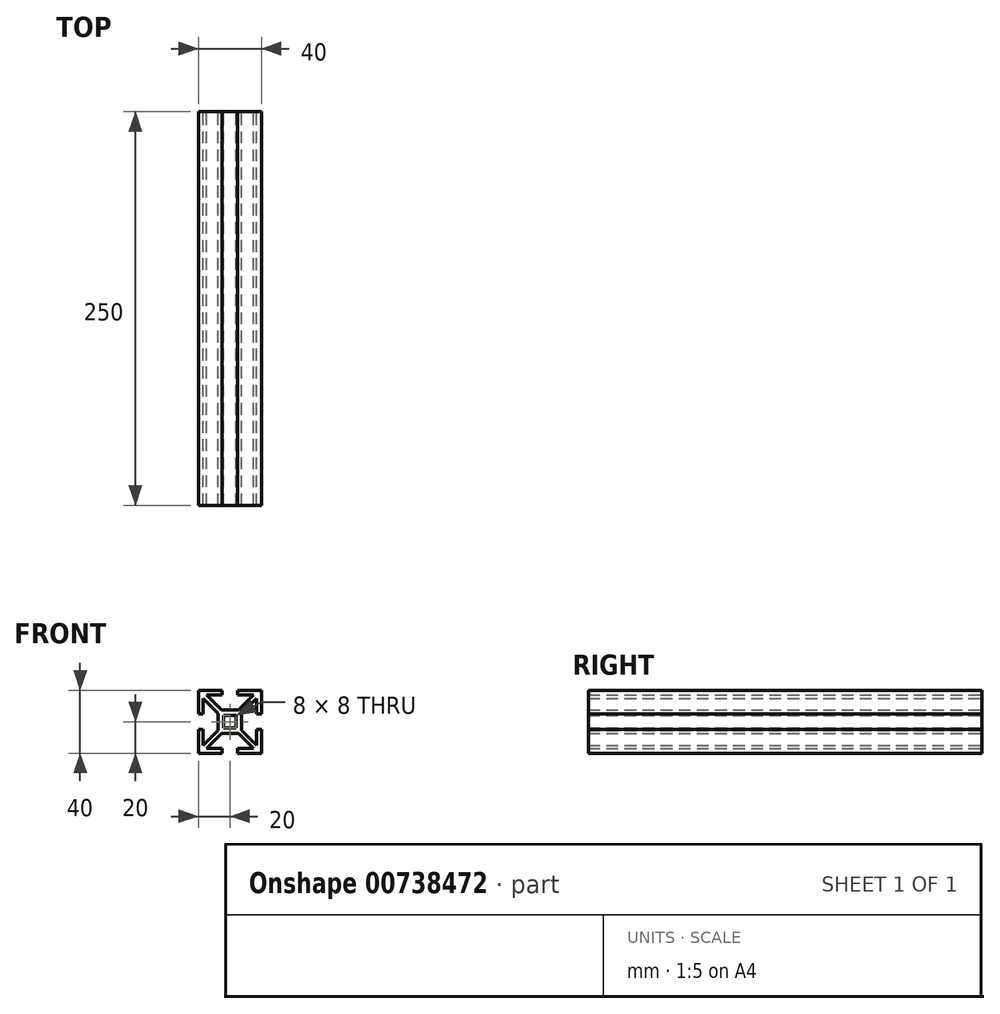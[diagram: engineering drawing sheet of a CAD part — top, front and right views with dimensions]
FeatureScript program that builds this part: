
annotation { "Feature Type Name" : "Feature", "Feature Type Description" : "" }
export const myFeature = defineFeature(function(context is Context, id is Id, definition is map)
    precondition{}
    {
        {
            var Q0;
            Q0=qCreatedBy(makeId("Front.planeOp"),FACE);
            var sketch = newSketch(context, id + "F0", { "sketchPlane" : qUnion([Q0])});
            skPoint(sketch, "E0.middle", {"position": v(0, 0) * mm});
            skLineSegment(sketch, "E1.bottom", {"start": v(20, 20) * mm, "end": v(-20, 20) * mm});
            skLineSegment(sketch, "E1.top", {"start": v(20, -20) * mm, "end": v(-20, -20) * mm});
            skLineSegment(sketch, "E1.left", {"start": v(20, 20) * mm, "end": v(20, -20) * mm});
            skLineSegment(sketch, "E1.right", {"start": v(-20, 20) * mm, "end": v(-20, -20) * mm});
            skLineSegment(sketch, "E2.bottom", {"start": v(4, 4) * mm, "end": v(-4, 4) * mm});
            skLineSegment(sketch, "E2.top", {"start": v(4, -4) * mm, "end": v(-4, -4) * mm});
            skLineSegment(sketch, "E2.left", {"start": v(4, 4) * mm, "end": v(4, -4) * mm});
            skLineSegment(sketch, "E2.right", {"start": v(-4, 4) * mm, "end": v(-4, -4) * mm});
            skLineSegment(sketch, "E3.bottom", {"start": v(7.5, -7.5) * mm, "end": v(-7.5, -7.5) * mm});
            skLineSegment(sketch, "E3.top", {"start": v(7.5, 7.5) * mm, "end": v(-7.5, 7.5) * mm});
            skLineSegment(sketch, "E3.left", {"start": v(7.5, -7.5) * mm, "end": v(7.5, 7.5) * mm});
            skLineSegment(sketch, "E3.right", {"start": v(-7.5, -7.5) * mm, "end": v(-7.5, 7.5) * mm});
            skLineSegment(sketch, "E4", {"start": v(-5, 20) * mm, "end": v(-5, -20) * mm, "construction": true});
            skLineSegment(sketch, "E5", {"start": v(5, -20) * mm, "end": v(5, 20) * mm, "construction": true});
            skLineSegment(sketch, "E6", {"start": v(-20, 5) * mm, "end": v(20, 5) * mm, "construction": true});
            skLineSegment(sketch, "E7", {"start": v(-20, -5) * mm, "end": v(20, -5) * mm, "construction": true});
            skLineSegment(sketch, "E8.bottom", {"start": v(17, 17) * mm, "end": v(-17, 17) * mm});
            skLineSegment(sketch, "E8.top", {"start": v(17, -17) * mm, "end": v(-17, -17) * mm});
            skLineSegment(sketch, "E8.left", {"start": v(17, 17) * mm, "end": v(17, -17) * mm});
            skLineSegment(sketch, "E8.right", {"start": v(-17, 17) * mm, "end": v(-17, -17) * mm});
            skLineSegment(sketch, "E9", {"start": v(0, 0) * mm, "end": v(20, 20) * mm, "construction": true});
            skLineSegment(sketch, "E10", {"start": v(0, 0) * mm, "end": v(20, -20) * mm, "construction": true});
            skLineSegment(sketch, "E11", {"start": v(0, 0) * mm, "end": v(-20, -20) * mm, "construction": true});
            skLineSegment(sketch, "E12", {"start": v(0, 0) * mm, "end": v(-20, 20) * mm, "construction": true});
            skLineSegment(sketch, "E13", {"start": v(5.38, 7.5) * mm, "end": v(14.88, 17) * mm});
            skLineSegment(sketch, "E14", {"start": v(7.5, 5.38) * mm, "end": v(17, 14.88) * mm});
            skLineSegment(sketch, "E15", {"start": v(7.5, -5.38) * mm, "end": v(17, -14.88) * mm});
            skLineSegment(sketch, "E16", {"start": v(5.38, -7.5) * mm, "end": v(14.88, -17) * mm});
            skLineSegment(sketch, "E17", {"start": v(-7.5, -5.38) * mm, "end": v(-17, -14.88) * mm});
            skLineSegment(sketch, "E18", {"start": v(-14.88, -17) * mm, "end": v(-5.38, -7.5) * mm});
            skLineSegment(sketch, "E19", {"start": v(-5.38, 7.5) * mm, "end": v(-14.88, 17) * mm});
            skLineSegment(sketch, "E20", {"start": v(-7.5, 5.38) * mm, "end": v(-17, 14.88) * mm});
            skLineSegment(sketch, "E21", {"start": v(-5, 20) * mm, "end": v(-5, 17) * mm});
            skLineSegment(sketch, "E22", {"start": v(5, 20) * mm, "end": v(5, 17) * mm});
            skLineSegment(sketch, "E23", {"start": v(17, 5) * mm, "end": v(20, 5) * mm});
            skLineSegment(sketch, "E24", {"start": v(17, -5) * mm, "end": v(20, -5) * mm});
            skLineSegment(sketch, "E25", {"start": v(5, -17) * mm, "end": v(5, -20) * mm});
            skLineSegment(sketch, "E26", {"start": v(-5, -17) * mm, "end": v(-5, -20) * mm});
            skLineSegment(sketch, "E27", {"start": v(-17, -5) * mm, "end": v(-20, -5) * mm});
            skLineSegment(sketch, "E28", {"start": v(-17, 5) * mm, "end": v(-20, 5) * mm});
            skSolve(sketch);
        }
        {
            var Q0;
            {var subQ2=sQuery(id+"F0.wireOp",EDGE,"E21");Q0=makeQuery(id+"F0.imprint","IMPRINT",FACE,{"disambiguationData":[TD([[makeQuery(id+"F0.imprint","IMPRINT",EDGE,{"derivedFrom":subQ2}),-1.0]])]});}
            var Q1;
            {var subQ4=sQuery(id+"F0.wireOp",EDGE,"E26");Q1=makeQuery(id+"F0.imprint","IMPRINT",FACE,{"disambiguationData":[TD([[makeQuery(id+"F0.imprint","IMPRINT",EDGE,{"derivedFrom":subQ4}),-1.0]])]});}
            var Q2;
            {var subQ8=sQuery(id+"F0.wireOp",EDGE,"E24");Q2=makeQuery(id+"F0.imprint","IMPRINT",FACE,{"disambiguationData":[TD([[makeQuery(id+"F0.imprint","IMPRINT",EDGE,{"derivedFrom":subQ8}),-1.0]])]});}
            var Q3;
            {var subQ2=sQuery(id+"F0.wireOp",EDGE,"E22");Q3=makeQuery(id+"F0.imprint","IMPRINT",FACE,{"disambiguationData":[TD([[makeQuery(id+"F0.imprint","IMPRINT",EDGE,{"derivedFrom":subQ2}),1.0]])]});}
            var Q4;
            {var subQ4=sQuery(id+"F0.wireOp",EDGE,"E13");Q4=makeQuery(id+"F0.imprint","IMPRINT",FACE,{"disambiguationData":[TD([[makeQuery(id+"F0.imprint","IMPRINT",EDGE,{"derivedFrom":subQ4}),-1.0]])]});}
            var Q5;
            {var subQ4=sQuery(id+"F0.wireOp",EDGE,"E19");Q5=makeQuery(id+"F0.imprint","IMPRINT",FACE,{"disambiguationData":[TD([[makeQuery(id+"F0.imprint","IMPRINT",EDGE,{"derivedFrom":subQ4}),1.0]])]});}
            var Q6;
            {var subQ3=sQuery(id+"F0.wireOp",EDGE,"E17");Q6=makeQuery(id+"F0.imprint","IMPRINT",FACE,{"disambiguationData":[TD([[makeQuery(id+"F0.imprint","IMPRINT",EDGE,{"derivedFrom":subQ3}),1.0]])]});}
            var Q7;
            {var subQ7=sQuery(id+"F0.wireOp",EDGE,"E15");Q7=makeQuery(id+"F0.imprint","IMPRINT",FACE,{"disambiguationData":[TD([[makeQuery(id+"F0.imprint","IMPRINT",EDGE,{"derivedFrom":subQ7}),-1.0]])]});}
            var Q8;
            Q8=makeQuery(id+"F0.imprint","IMPRINT",FACE,{"disambiguationData":[TD([[makeQuery(id+"F0.imprint","IMPRINT",EDGE,{"derivedFrom":sQuery(id+"F0.wireOp",EDGE,"E2.bottom")}),-1.0]])]});
            extrude(context, id + "F1", {"entities" : qUnion([Q0, Q1, Q2, Q3, Q4, Q5, Q6, Q7, Q8]), "endBound" : BoundingType.SYMMETRIC, "depth" : 250 * mm, "offsetDistance" : 25 * mm});
        }
    });
